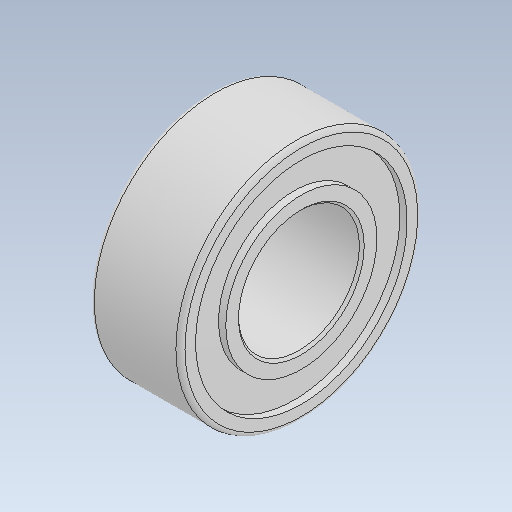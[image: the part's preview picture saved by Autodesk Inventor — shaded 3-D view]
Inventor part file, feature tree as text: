
AUTODESK INVENTOR PART (.ipt)
format: ipt  version: 2020 (Build 240168000, 168)  size: 151,040 bytes
history: native  units: in
note: dims shown in document units (in); Inventor stores cm internally (conversion verified against a paired STEP export)
features: chamfer x1
ambient origin geometry x8: Origin, YZ Plane, XZ Plane, XY Plane, X Axis, Y Axis, Z Axis, Center Point
bodies: Solid1 (feature_tree)
feature tree (1):
  chamfer  "Chamfer1"  [1 undecoded]
note: 1 required parameter value undecoded (feature->parameter linkage not recoverable at this tier; creation-order binding heuristic only, values carry confidence <= 0.55)
